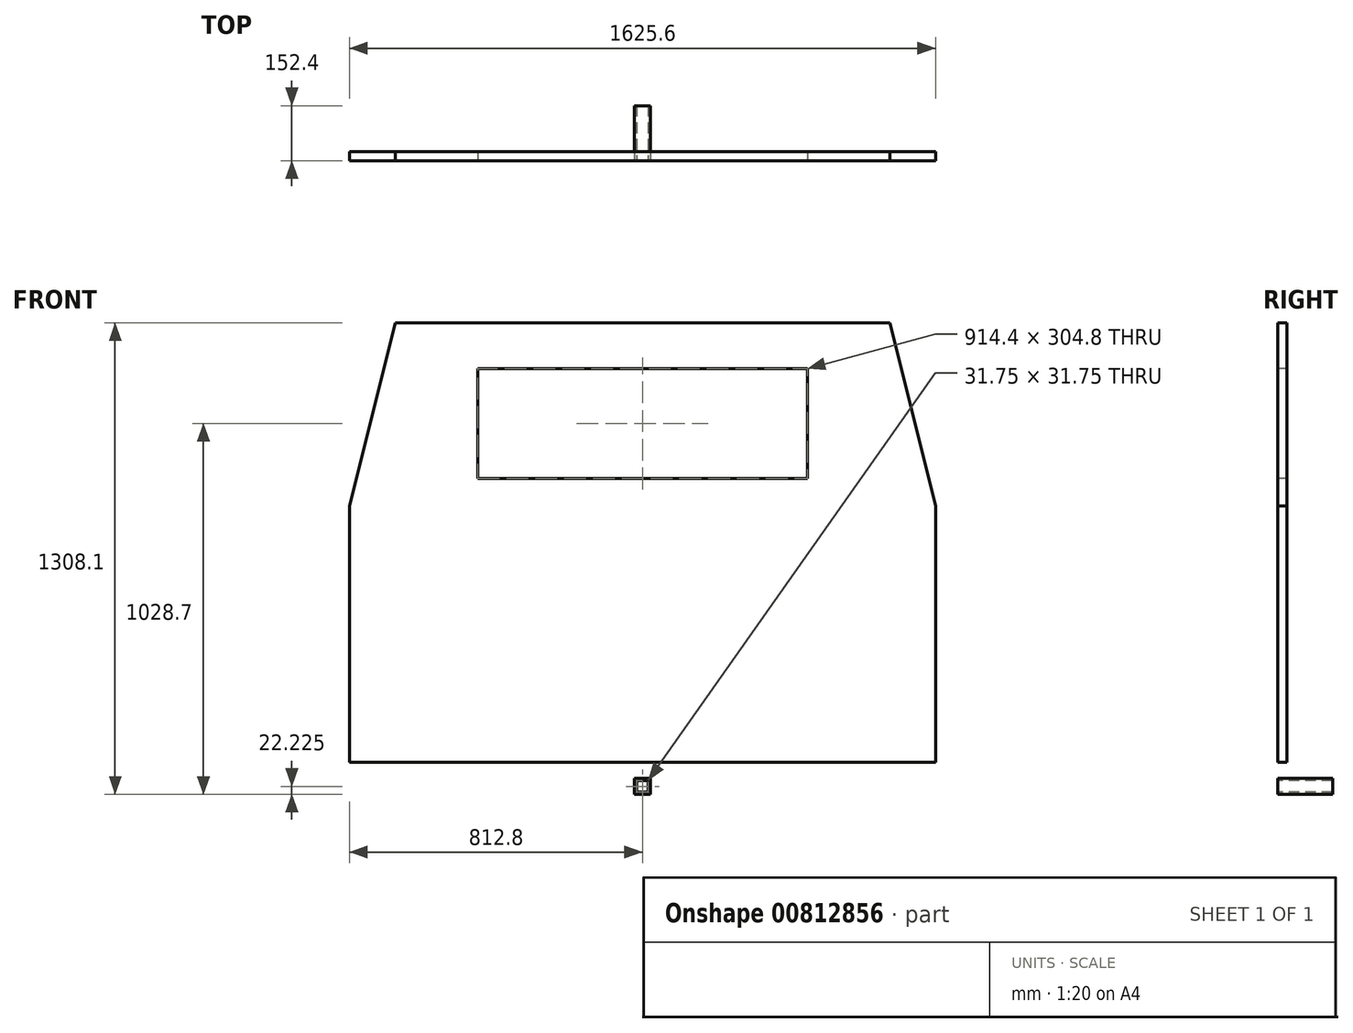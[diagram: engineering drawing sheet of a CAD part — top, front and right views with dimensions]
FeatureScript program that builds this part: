
annotation { "Feature Type Name" : "Feature", "Feature Type Description" : "" }
export const myFeature = defineFeature(function(context is Context, id is Id, definition is map)
    precondition{}
    {
        {
            var Q0;
            Q0=qCreatedBy(makeId("Front.planeOp"),FACE);
            var sketch = newSketch(context, id + "F0", { "sketchPlane" : qUnion([Q0])});
            skLineSegment(sketch, "E0", {"start": v(0, 0) * mm, "end": v(-812.8, 0) * mm});
            skLineSegment(sketch, "E1", {"start": v(-812.8, 0) * mm, "end": v(-812.8, 711.2) * mm});
            skLineSegment(sketch, "E2", {"start": v(0, 0) * mm, "end": v(812.8, 0) * mm});
            skLineSegment(sketch, "E3", {"start": v(812.8, 0) * mm, "end": v(812.8, 711.2) * mm});
            skLineSegment(sketch, "E4", {"start": v(812.8, 711.2) * mm, "end": v(685.8, 1219.2) * mm});
            skLineSegment(sketch, "E5", {"start": v(685.8, 1219.2) * mm, "end": v(-685.8, 1219.2) * mm});
            skLineSegment(sketch, "E6", {"start": v(-685.8, 1219.2) * mm, "end": v(-812.8, 711.2) * mm});
            skLineSegment(sketch, "E7.bottom", {"start": v(-457.2, 1092.2) * mm, "end": v(457.2, 1092.2) * mm});
            skLineSegment(sketch, "E7.top", {"start": v(-457.2, 787.4) * mm, "end": v(457.2, 787.4) * mm});
            skLineSegment(sketch, "E7.left", {"start": v(-457.2, 1092.2) * mm, "end": v(-457.2, 787.4) * mm});
            skLineSegment(sketch, "E7.right", {"start": v(457.2, 1092.2) * mm, "end": v(457.2, 787.4) * mm});
            skLineSegment(sketch, "E8", {"start": v(-736.6, 1016) * mm, "end": v(-736.6, 228.6) * mm});
            skLineSegment(sketch, "E9", {"start": v(-736.6, 228.6) * mm, "end": v(736.6, 228.6) * mm});
            skLineSegment(sketch, "E10", {"start": v(736.6, 228.6) * mm, "end": v(736.6, 1016) * mm});
            skLineSegment(sketch, "E11.bottom", {"start": v(-15.87, -50.8) * mm, "end": v(15.88, -50.8) * mm});
            skLineSegment(sketch, "E11.top", {"start": v(-15.87, -82.55) * mm, "end": v(15.88, -82.55) * mm});
            skLineSegment(sketch, "E11.left", {"start": v(-15.87, -50.8) * mm, "end": v(-15.87, -82.55) * mm});
            skLineSegment(sketch, "E11.right", {"start": v(15.88, -50.8) * mm, "end": v(15.88, -82.55) * mm});
            skLineSegment(sketch, "E12.bottom", {"start": v(-22.22, -44.45) * mm, "end": v(22.23, -44.45) * mm});
            skLineSegment(sketch, "E12.top", {"start": v(-22.22, -88.9) * mm, "end": v(22.23, -88.9) * mm});
            skLineSegment(sketch, "E12.left", {"start": v(-22.22, -44.45) * mm, "end": v(-22.22, -88.9) * mm});
            skLineSegment(sketch, "E12.right", {"start": v(22.23, -44.45) * mm, "end": v(22.23, -88.9) * mm});
            skSolve(sketch);
        }
        {
            var Q0;
            Q0=makeQuery(id+"F0.imprint","IMPRINT",FACE,{"disambiguationData":[TD([[makeQuery(id+"F0.imprint","IMPRINT",EDGE,{"derivedFrom":sQuery(id+"F0.wireOp",EDGE,"E11.bottom")}),1.0]])]});
            extrude(context, id + "F1", {"entities" : qUnion([Q0]), "depth" : -152.4 * mm, "offsetDistance" : 25.4 * mm});
        }
        {
            var Q0;
            Q0=makeQuery(id+"F0.imprint","IMPRINT",FACE,{"disambiguationData":[TD([[makeQuery(id+"F0.imprint","IMPRINT",EDGE,{"derivedFrom":sQuery(id+"F0.wireOp",EDGE,"E0")}),-1.0]])]});
            var Q1;
            {var subQ1=sQuery(id+"F0.wireOp",EDGE,"E5");Q1=makeQuery(id+"F0.imprint","IMPRINT",FACE,{"disambiguationData":[TD([[makeQuery(id+"F0.imprint","IMPRINT",EDGE,{"derivedFrom":subQ1}),1.0]])]});}
            extrude(context, id + "F2", {"entities" : qUnion([Q0, Q1]), "depth" : -25.4 * mm, "offsetDistance" : 25.4 * mm});
        }
    });
